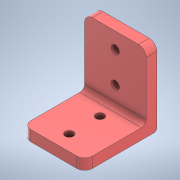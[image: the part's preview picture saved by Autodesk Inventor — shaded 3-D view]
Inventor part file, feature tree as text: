
AUTODESK INVENTOR PART (.ipt)
format: ipt  version: 2022 (Build 260153000, 153)  size: 152,064 bytes
history: native  units: mm
features: sketch x4, extrude x2, hole x2, fillet x1
ambient origin geometry x8: Origin, YZ Plane, XZ Plane, XY Plane, X Axis, Y Axis, Z Axis, Center Point
bodies: Solid1 (feature_tree)
feature tree (9):
  extrude  "Extrusion1"  Depth=40.0mm
  sketch  "Sketch2"  dims[d2=7.0mm d3=0.0mm d4=20.0mm d5=10.0mm]
  extrude  "Extrusion2"  Depth=10.0mm
  fillet  "Fillet2"  Radius=10.0mm
  hole  "Hole4"  [1 undecoded]
  hole  "Hole5"  [1 undecoded]
  sketch  "Sketch1"  dims[d0=40.0mm d1=40.0mm]
  sketch  "Sketch3"  dims[d14=50.0mm d15=40.0mm]
  sketch  "Sketch4"  dims[d16=7.0mm d17=0.0mm d19=3.0mm d20=5.0mm d21=2.0mm d22=20.0mm d23=12.5mm d38=5.4mm d39=6.0mm d40=4.0mm d41=2.0mm d42=90.0deg d43=8.0mm d44=20.594885mm d45=5.4mm d46=6.0mm d47=4.0mm d48=2.0mm d49=90.0deg d50=8.0mm d51=20.594885mm]
note: 2 required parameter values undecoded (feature->parameter linkage not recoverable at this tier; creation-order binding heuristic only, values carry confidence <= 0.55)
